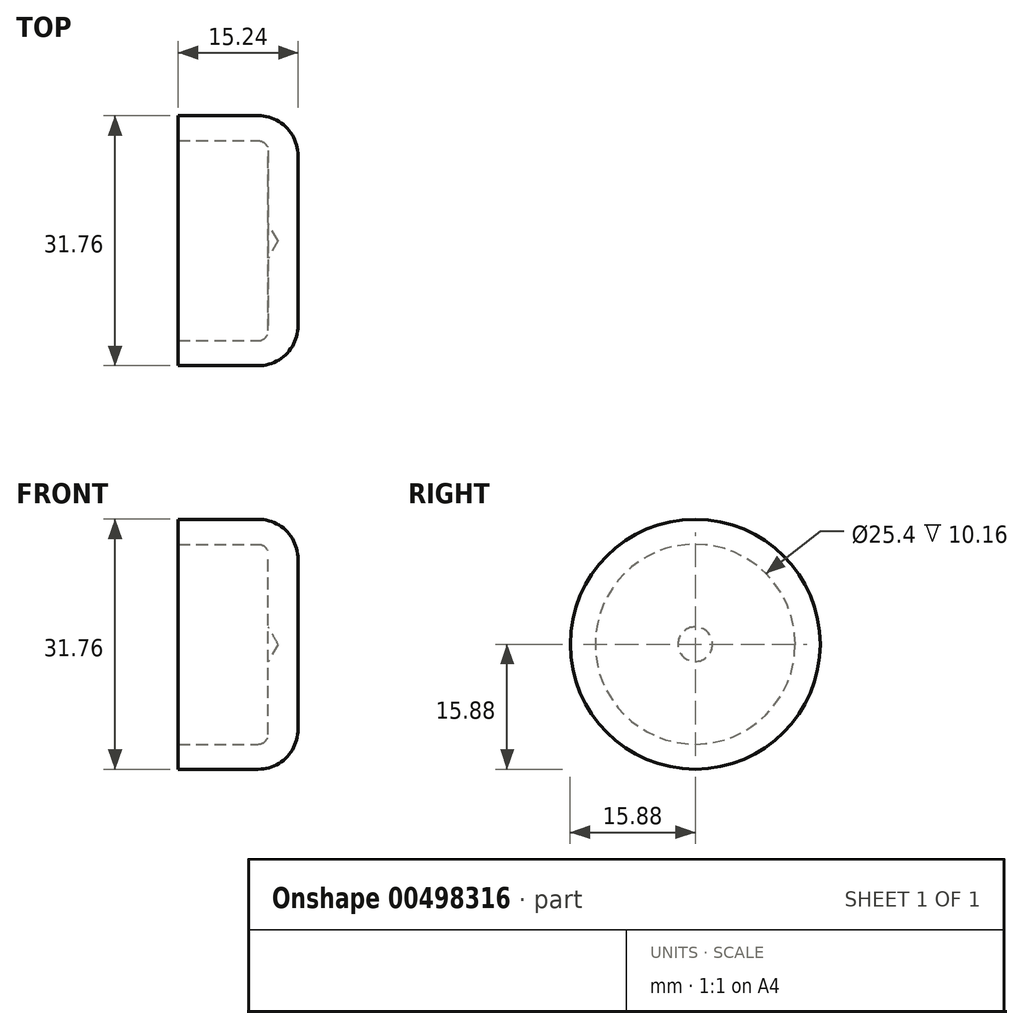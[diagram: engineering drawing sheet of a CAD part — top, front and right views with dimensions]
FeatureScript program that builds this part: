
annotation { "Feature Type Name" : "Feature", "Feature Type Description" : "" }
export const myFeature = defineFeature(function(context is Context, id is Id, definition is map)
    precondition{}
    {
        {
            var Q0;
            Q0=qCreatedBy(makeId("Right.planeOp"),FACE);
            var sketch = newSketch(context, id + "F0", { "sketchPlane" : qUnion([Q0])});
            skCircle(sketch, "E0", {"center": v(0, 0) * mm, "radius": 15.88 * mm});
            skSolve(sketch);
        }
        {
            var Q0;
            Q0 = qSketchRegion(id + "F0", true);
            extrude(context, id + "F1", {"entities" : qUnion([Q0]), "depth" : 15.24 * mm, "offsetDistance" : 25.4 * mm});
        }
        {
            var Q0;
            Q0=makeQuery(id+"F1.opExtrude","CAP_EDGE",EDGE,{"disambiguationData":[OSD([sQuery(id+"F0.wireOp",EDGE,"E0")])],"isStart":false});
            fillet(context, id + "F2", {"entities" : qUnion([Q0]), "radius" : 5.08 * mm, "tangentPropagation" : true, "allowEdgeOverflow" : false});
        }
        {
            var Q0;
            Q0=qCreatedBy(makeId("Front.planeOp"),FACE);
            var sketch = newSketch(context, id + "F3", { "sketchPlane" : qUnion([Q0])});
            skLineSegment(sketch, "E1", {"start": v(0, 0) * mm, "end": v(0, 12.7) * mm});
            skLineSegment(sketch, "E2", {"start": v(0, 12.7) * mm, "end": v(10.16, 12.7) * mm});
            skLineSegment(sketch, "E3", {"start": v(11.43, 2.2) * mm, "end": v(12.7, 0) * mm});
            skLineSegment(sketch, "E4", {"start": v(11.43, 11.43) * mm, "end": v(11.43, 2.2) * mm});
            skPoint(sketch, "E5.visualSharp", {"position": v(11.43, 12.7) * mm});
            skArc(sketch, "E5.filletArc", {"start": v(11.43, 11.43) * mm, "mid": v(11.06, 12.33) * mm, "end": v(10.16, 12.7) * mm});
            skLineSegment(sketch, "E6", {"start": v(0, 0) * mm, "end": v(12.7, 0) * mm});
            skSolve(sketch);
        }
        {
            var Q0;
            Q0 = qSketchRegion(id + "F3", true);
            var Q1;
            Q1=sQuery(id+"F3.wireOp",EDGE,"E6");
            revolve(context, id + "F4", {"operationType" : NewBodyOperationType.REMOVE, "entities" : qUnion([Q0]), "axis" : qUnion([Q1]), "revolveType" : RevolveType.FULL, "oppositeDirection" : true});
        }
    });
